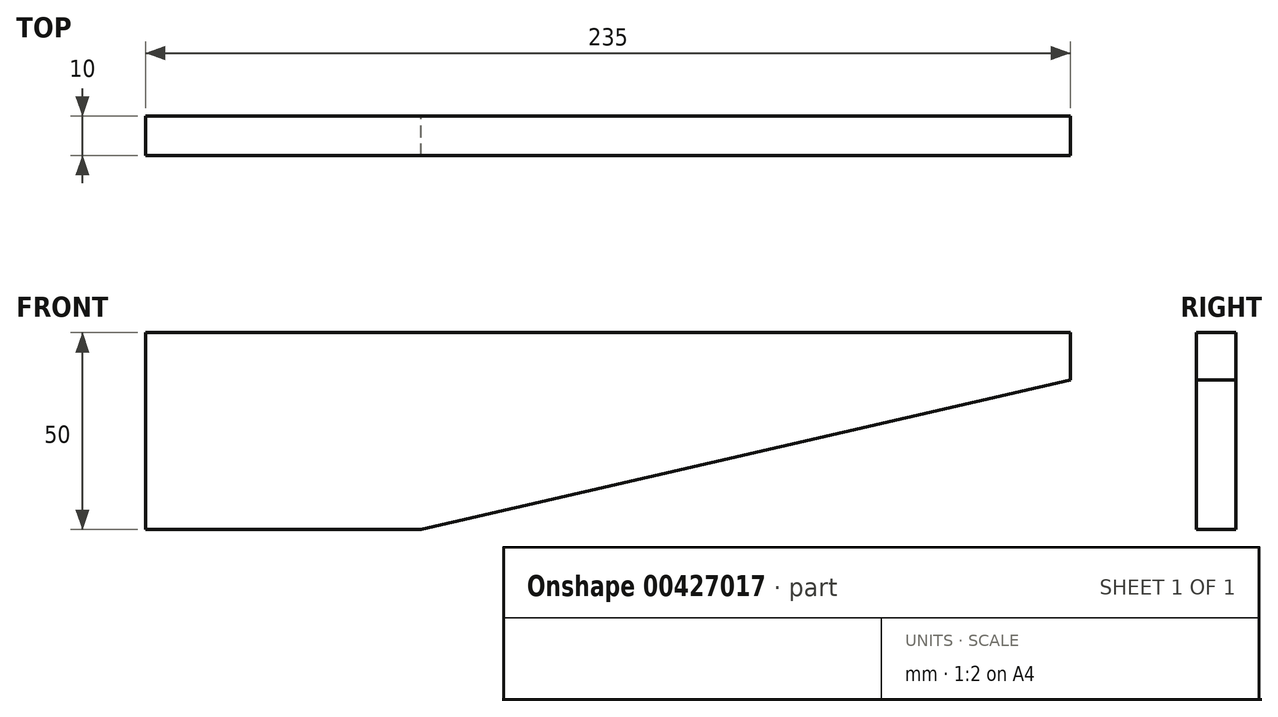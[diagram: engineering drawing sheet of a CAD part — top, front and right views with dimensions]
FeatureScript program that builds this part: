
annotation { "Feature Type Name" : "Feature", "Feature Type Description" : "" }
export const myFeature = defineFeature(function(context is Context, id is Id, definition is map)
    precondition{}
    {
        {
            var Q0;
            Q0=qCreatedBy(makeId("Front.planeOp"),FACE);
            var sketch = newSketch(context, id + "F0", { "sketchPlane" : qUnion([Q0])});
            skLineSegment(sketch, "E0", {"start": v(0, 0) * mm, "end": v(0, 50) * mm});
            skLineSegment(sketch, "E1", {"start": v(0, 50) * mm, "end": v(235, 50) * mm});
            skLineSegment(sketch, "E2", {"start": v(235, 50) * mm, "end": v(235, 38) * mm});
            skLineSegment(sketch, "E3", {"start": v(235, 38) * mm, "end": v(70, 0) * mm});
            skLineSegment(sketch, "E4", {"start": v(70, 0) * mm, "end": v(0, 0) * mm});
            skSolve(sketch);
        }
        {
            var Q0;
            Q0=makeQuery(id+"F0.imprint","IMPRINT",FACE,{"disambiguationData":[TD([[makeQuery(id+"F0.imprint","IMPRINT",EDGE,{"derivedFrom":sQuery(id+"F0.wireOp",EDGE,"E0")}),-1.0]])]});
            extrude(context, id + "F1", {"entities" : qUnion([Q0]), "endBound" : BoundingType.SYMMETRIC, "depth" : 10 * mm});
        }
    });
